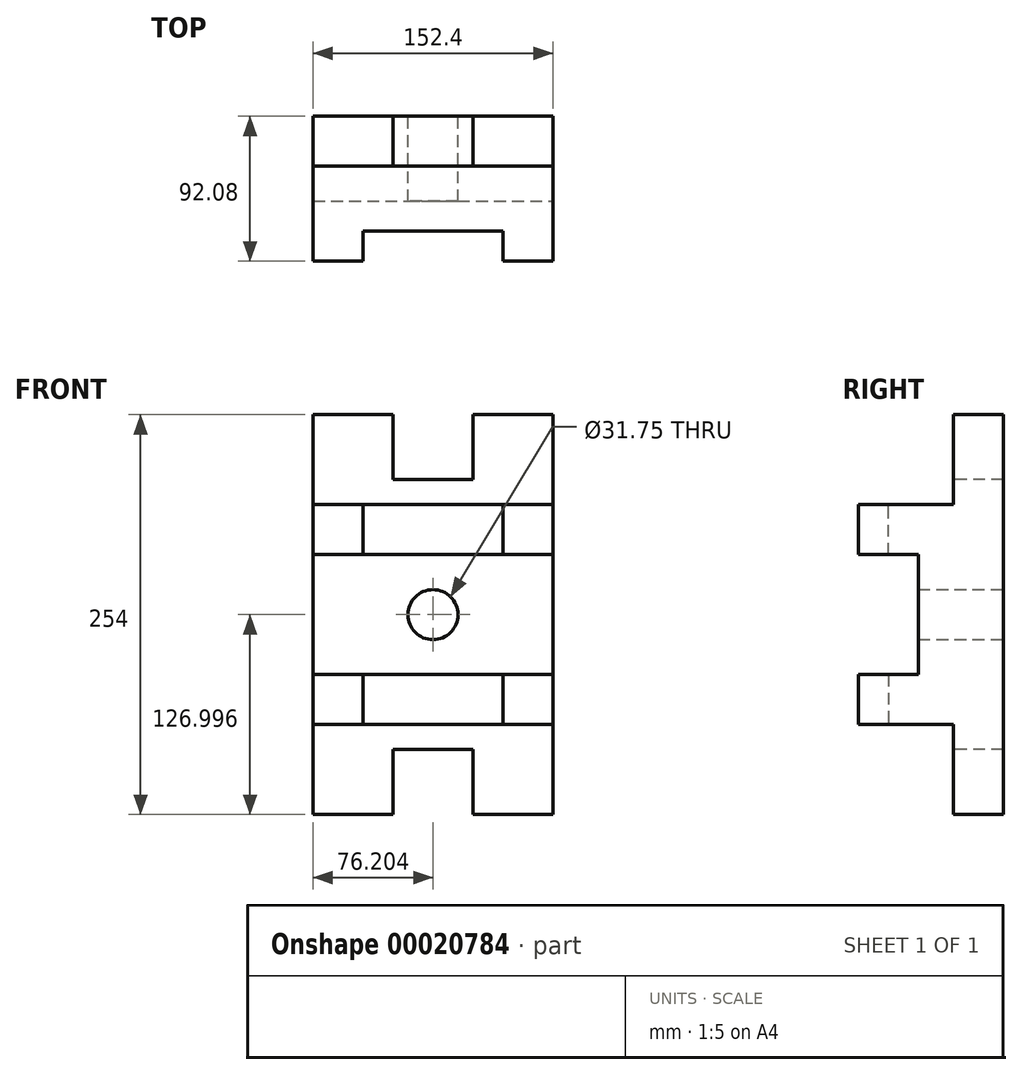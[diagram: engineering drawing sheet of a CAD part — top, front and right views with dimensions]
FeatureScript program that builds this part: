
annotation { "Feature Type Name" : "Feature", "Feature Type Description" : "" }
export const myFeature = defineFeature(function(context is Context, id is Id, definition is map)
    precondition{}
    {
        {
            var Q0;
            Q0=qCreatedBy(makeId("Front.planeOp"),FACE);
            var sketch = newSketch(context, id + "F0", { "sketchPlane" : qUnion([Q0])});
            skLineSegment(sketch, "E0.bottom", {"start": v(-36.72, 108.22) * mm, "end": v(39.48, 108.22) * mm});
            skLineSegment(sketch, "E0.top", {"start": v(-36.72, -18.78) * mm, "end": v(39.48, -18.78) * mm});
            skLineSegment(sketch, "E0.left", {"start": v(-36.72, 108.22) * mm, "end": v(-36.72, -18.78) * mm});
            skLineSegment(sketch, "E0.right", {"start": v(39.48, 108.22) * mm, "end": v(39.48, -18.78) * mm});
            skSolve(sketch);
        }
        {
            var Q0;
            Q0=makeQuery(id+"F0.imprint","IMPRINT",FACE,{"disambiguationData":[TD([[makeQuery(id+"F0.imprint","IMPRINT",EDGE,{"derivedFrom":sQuery(id+"F0.wireOp",EDGE,"E0.bottom")}),-1.0]])]});
            var Q1;
            Q1 = qSketchRegion(id + "F2", true);
            extrude(context, id + "F1", {"entities" : qUnion([Q0, Q1]), "depth" : 31.75 * mm});
        }
        {
            var Q0;
            Q0=makeQuery(id+"F1.opExtrude","CAP_FACE",FACE,{"disambiguationData":[OSD([sQuery(id+"F0.wireOp",EDGE,"E0.bottom"),sQuery(id+"F0.wireOp",EDGE,"E0.top"),sQuery(id+"F0.wireOp",EDGE,"E0.left"),sQuery(id+"F0.wireOp",EDGE,"E0.right")])],"isStart":false});
            var sketch = newSketch(context, id + "F2", { "sketchPlane" : qUnion([Q0])});
            skLineSegment(sketch, "E1", {"start": v(-36.72, 108.22) * mm, "end": v(-36.72, 70.12) * mm});
            skLineSegment(sketch, "E2", {"start": v(-36.72, 70.12) * mm, "end": v(-36.72, 38.37) * mm});
            skLineSegment(sketch, "E3", {"start": v(-36.72, -18.78) * mm, "end": v(14.08, -18.78) * mm});
            skLineSegment(sketch, "E4", {"start": v(-36.72, 70.12) * mm, "end": v(39.48, 70.12) * mm});
            skLineSegment(sketch, "E5", {"start": v(-36.72, 38.37) * mm, "end": v(39.48, 38.37) * mm});
            skLineSegment(sketch, "E6", {"start": v(14.08, -18.78) * mm, "end": v(14.08, 22.5) * mm});
            skLineSegment(sketch, "E7", {"start": v(14.08, 22.5) * mm, "end": v(39.48, 22.5) * mm});
            skCircle(sketch, "E8", {"center": v(39.48, 108.22) * mm, "radius": 15.88 * mm});
            skLineSegment(sketch, "E9", {"start": v(-36.72, 108.22) * mm, "end": v(-4.97, 108.22) * mm});
            skLineSegment(sketch, "E10", {"start": v(-4.97, 70.12) * mm, "end": v(-4.97, 38.37) * mm});
            skSolve(sketch);
        }
        {
            var Q0;
            {var subQ2=sQuery(id+"F2.wireOp",EDGE,"E2");Q0=makeQuery(id+"F2.imprint","IMPRINT",FACE,{"disambiguationData":[TD([[makeQuery(id+"F2.imprint","IMPRINT",EDGE,{"derivedFrom":subQ2}),1.0]])]});}
            extrude(context, id + "F3", {"entities" : qUnion([Q0]), "depth" : 60.32 * mm});
        }
        {
            var Q0;
            {var subQ5=sQuery(id+"F2.wireOp",EDGE,"E10");Q0=makeQuery(id+"F2.imprint","IMPRINT",FACE,{"disambiguationData":[TD([[makeQuery(id+"F2.imprint","IMPRINT",EDGE,{"derivedFrom":subQ5}),1.0]])]});}
            extrude(context, id + "F4", {"entities" : qUnion([Q0]), "depth" : 41.27 * mm});
        }
        {
            var Q0;
            {var subQ9=sQuery(id+"F2.wireOp",EDGE,"E1");Q0=makeQuery(id+"F2.imprint","IMPRINT",FACE,{"disambiguationData":[TD([[makeQuery(id+"F2.imprint","IMPRINT",EDGE,{"derivedFrom":subQ9}),1.0]])]});}
            extrude(context, id + "F5", {"entities" : qUnion([Q0]), "operationType" : NewBodyOperationType.ADD, "depth" : 22.22 * mm});
        }
        {
            var Q0;
            {var subQ1=sQuery(id+"F2.wireOp",EDGE,"E8");var subQ3=makeQuery(id+"F1.opExtrude","CAP_EDGE",EDGE,{"disambiguationData":[OSD([sQuery(id+"F0.wireOp",EDGE,"E0.bottom")])],"isStart":false});var subQ5=makeQuery(id+"F2.imprint","INTERSECT",VERTEX,{"derivedFrom":[subQ3,subQ1]});Q0=makeQuery(id+"F2.imprint","IMPRINT",FACE,{"disambiguationData":[TD([[makeQuery(id+"F2.imprint","IMPRINT",EDGE,{"disambiguationData":[TD([[subQ5,-1.0]])],"derivedFrom":subQ1}),1.0]])]});}
            extrude(context, id + "F6", {"entities" : qUnion([Q0]), "operationType" : NewBodyOperationType.REMOVE, "oppositeDirection" : true, "depth" : 31.75 * mm});
        }
        {
            var Q0;
            {var subQ4=sQuery(id+"F2.wireOp",EDGE,"E6");Q0=makeQuery(id+"F2.imprint","IMPRINT",FACE,{"disambiguationData":[TD([[makeQuery(id+"F2.imprint","IMPRINT",EDGE,{"derivedFrom":subQ4}),-1.0]])]});}
            extrude(context, id + "F7", {"entities" : qUnion([Q0]), "operationType" : NewBodyOperationType.REMOVE, "oppositeDirection" : true, "depth" : 31.75 * mm});
        }
        {
            var Q0;
            Q0=makeQuery(id+"F3.opExtrude","SWEPT_BODY",BODY,{"disambiguationData":[OSD([sQuery(id+"F2.wireOp",EDGE,"E2"),sQuery(id+"F2.wireOp",EDGE,"E4"),sQuery(id+"F2.wireOp",EDGE,"E5"),sQuery(id+"F2.wireOp",EDGE,"E10")])]});
            var Q1;
            Q1=makeQuery(id+"F1.opExtrude","SWEPT_BODY",BODY,{"disambiguationData":[OSD([sQuery(id+"F0.wireOp",EDGE,"E0.bottom"),sQuery(id+"F0.wireOp",EDGE,"E0.top"),sQuery(id+"F0.wireOp",EDGE,"E0.left"),sQuery(id+"F0.wireOp",EDGE,"E0.right")])]});
            var Q2;
            Q2=makeQuery(id+"F4.opExtrude","SWEPT_BODY",BODY,{"disambiguationData":[OSD([sQuery(id+"F0.wireOp",EDGE,"E0.right"),sQuery(id+"F2.wireOp",EDGE,"E4"),sQuery(id+"F2.wireOp",EDGE,"E5"),sQuery(id+"F2.wireOp",EDGE,"E10")])]});
            var Q3;
            {var subQ0=sQuery(id+"F0.wireOp",EDGE,"E0.right");Q3=makeQuery(id+"F5.boolean.opBoolean","MERGE",FACE,{"derivedFrom":[makeQuery(id+"F1.opExtrude","SWEPT_FACE",FACE,{"disambiguationData":[OSD([subQ0])]}),makeQuery(id+"F5.opExtrude","SWEPT_FACE",FACE,{"disambiguationData":[OSD([subQ0])]})]});}
            mirror(context, id + "F8", {"operationType" : NewBodyOperationType.ADD, "entities" : qUnion([Q0, Q1, Q2]), "mirrorPlane" : qUnion([Q3])});
        }
        {
            var Q0;
            Q0=makeQuery(id+"F1.opExtrude","SWEPT_BODY",BODY,{"disambiguationData":[OSD([sQuery(id+"F0.wireOp",EDGE,"E0.bottom"),sQuery(id+"F0.wireOp",EDGE,"E0.top"),sQuery(id+"F0.wireOp",EDGE,"E0.left"),sQuery(id+"F0.wireOp",EDGE,"E0.right")])]});
            var Q1;
            Q1=makeQuery(id+"F3.opExtrude","SWEPT_BODY",BODY,{"disambiguationData":[OSD([sQuery(id+"F2.wireOp",EDGE,"E2"),sQuery(id+"F2.wireOp",EDGE,"E4"),sQuery(id+"F2.wireOp",EDGE,"E5"),sQuery(id+"F2.wireOp",EDGE,"E10")])]});
            var Q2;
            {var subQ0=sQuery(id+"F0.wireOp",EDGE,"E0.bottom");Q2=makeQuery(id+"F8.opPattern","COPY",FACE,{"derivedFrom":makeQuery(id+"F5.boolean.opBoolean","MERGE",FACE,{"derivedFrom":[makeQuery(id+"F1.opExtrude","SWEPT_FACE",FACE,{"disambiguationData":[OSD([subQ0])]}),makeQuery(id+"F5.opExtrude","SWEPT_FACE",FACE,{"disambiguationData":[OSD([subQ0,sQuery(id+"F2.wireOp",EDGE,"E9")])]})]}),"instanceName":"1"});}
            mirror(context, id + "F9", {"operationType" : NewBodyOperationType.ADD, "entities" : qUnion([Q0, Q1]), "mirrorPlane" : qUnion([Q2])});
        }
    });
